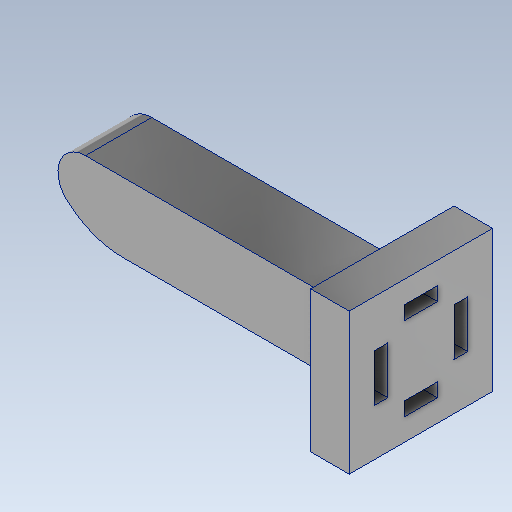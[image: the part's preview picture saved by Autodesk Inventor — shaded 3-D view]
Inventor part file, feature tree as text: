
AUTODESK INVENTOR PART (.ipt)
format: ipt  version: 2025.2 (Build 292293000, 293)  size: 409,088 bytes
history: native  units: mm
features: extrude x4, sketch x4, fillet x2
ambient origin geometry x8: Origin, YZ Plane, XZ Plane, XY Plane, X Axis, Y Axis, Z Axis, Center Point
bodies: Solid2 (feature_tree)
feature tree (10):
  extrude  "Extrusion2"  Depth=12.6mm
  fillet  "Fillet2"  Radius=15.6mm
  fillet  "Rundung3"  Radius=12.6mm
  extrude  "Extrusion12"  Depth=5.0mm
  extrude  "Extrusion13"  Depth=37.5mm
  extrude  "Extrusion19"  Depth=3.0mm
  sketch  "Sketch5"  dims[d56=12.0mm d57=0.0mm d63=44.7mm d67=15.6mm d71=0.0mm d97=12.6mm]
  sketch  "Skizze17"  dims[d98=15.0mm d105=5.0mm]
  sketch  "Skizze18"  dims[d123=1.0mm d124=37.5mm]
  sketch  "Skizze22"  dims[d125=38.5mm d127=1.0mm d128=5.5mm d133=7.0mm d134=0.0mm d135=3.5mm d136=2.5mm d137=2.5mm d138=3.5mm d139=2.5mm d140=2.5mm d141=2.5mm d142=2.5mm d143=2.5mm d144=2.5mm d145=3.5mm d146=3.5mm d147=2.5mm d148=0.0mm d151=26.0mm d152=25.6mm d153=6.5mm d154=6.5mm d155=7.0mm d156=7.0mm d172=0.0mm d173=2.5mm d175=2.5mm d176=2.5mm d180=3.0mm d181=3.0mm d183=2.0mm d184=2.0mm d185=2.0mm d186=2.0mm d187=10.0mm d188=0.0mm d190=2.5mm d191=3.0mm d192=3.0mm]
